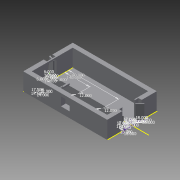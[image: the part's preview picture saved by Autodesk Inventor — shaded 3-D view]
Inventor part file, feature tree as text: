
AUTODESK INVENTOR PART (.ipt)
format: ipt  version: 2013 SP2 (Build 170200200, 200)  size: 399,872 bytes
history: native  units: in
note: dims shown in document units (in); Inventor stores cm internally (conversion verified against a paired STEP export)
features: extrude x18, sketch x11, projected_geometry x2
ambient origin geometry x8: Origin, YZ Plane, XZ Plane, XY Plane, X Axis, Y Axis, Z Axis, Center Point
feature tree (31):
  extrude  "Extrusion9"  Depth=132.0in
  extrude  "Extrusion10"  Depth=216.0in
  extrude  "Extrusion11"  Depth=24.0in
  extrude  "Extrusion12"  Depth=72.0in
  extrude  "Extrusion13"  Depth=24.0in
  extrude  "Extrusion15"  Depth=4.5in
  sketch  "Sketch15"  dims[d34=48.0in d35=114.0in]
  extrude  "Extrusion18"  Depth=168.0in
  extrude  "Extrusion19"  Depth=114.0in
  extrude  "Extrusion20"  Depth=35.0in
  extrude  "Extrusion21"  Depth=468.0in
  extrude  "Extrusion22"  Depth=1.0in TaperAngle=0.0deg
  extrude  "Extrusion23"  Depth=16.0in TaperAngle=0.0deg
  extrude  "Extrusion24"  Depth=7.5in
  extrude  "Extrusion25"  Depth=7.25in
  extrude  "Extrusion26"  Depth=28.5in
  extrude  "Extrusion16"  Depth=7.5in
  extrude  "Extrusion17"  Depth=7.25in
  extrude  "Extrusion14"  Depth=7.5in
  sketch  "Sketch1"  dims[d0=288.0in d1=480.0in d2=432.0in d3=240.0in d5=132.0in d7=150.0in]
  sketch  "Sketch8"  dims[d11=57.0in d17=216.0in]
  projected_geometry  "Projected Loop5"
  sketch  "Sketch9"  dims[d18=276.0in d19=24.0in]
  projected_geometry  "Projected Loop6"
  sketch  "Sketch10"  dims[d20=24.0in d23=72.0in]
  sketch  "Sketch11"  dims[d24=102.0in d25=24.0in]
  sketch  "Sketch12"  dims[d27=432.0in d28=4.5in]
  sketch  "Sketch14"  dims[d29=0.0in d30=168.0in]
  sketch  "Sketch16"  dims[d36=24.0in d46=35.0in]
  sketch  "Sketch17"  dims[d105=35.0in d106=468.0in]
  sketch  "Sketch18"  dims[d107=96.0in d108=0.0in d109=1.0in d110=0.0in d111=16.0in d112=0.0in d113=7.5in d115=7.25in d116=28.5in d117=7.5in d118=7.25in d119=7.5in d120=7.25in d121=7.5in d122=7.25in d123=7.5in d124=7.25in d125=7.5in d126=7.25in d127=7.5in d128=7.25in d129=7.5in d130=7.25in d131=7.5in d132=7.25in d133=7.5in d134=7.25in d135=7.5in d136=7.25in d137=7.5in d138=7.25in d139=7.5in d140=7.25in d141=7.5in d142=7.25in d143=16.0in d144=0.0in d145=48.0in d147=48.0in d148=32.0in d150=16.0in d151=0.0in d152=12.75in d153=0.0in d154=7.25in d155=7.5in d156=1.0in d158=1.0in d159=0.0in d161=12.0in d163=12.0in d164=140.0in d165=280.0in d166=12.0in d167=17.5in d168=17.5in d169=12.0in d172=17.0in d173=17.0in d174=8.5in d175=12.0in d176=17.0in d177=17.0in d178=8.5in d179=12.0in d180=17.0in d181=17.0in d182=8.5in d183=18.0in d184=18.0in d185=24.0in d186=2.0in d187=0.0in d188=3.0in d189=0.0in d190=1.0in d191=0.0in d192=6.0in d193=6.0in d194=6.0in d195=18.0in d196=18.0in d197=18.0in d198=18.0in d199=36.0in d200=6.0in d201=1.0in d202=0.0in d203=1.0in d204=0.0in d205=80.0in d206=0.0in d207=80.0in d208=0.0in d209=80.0in d210=0.0in d211=80.0in d212=0.0in d213=1.0in d214=0.0in d215=6.0in d216=36.0in d217=80.0in d218=0.0in]
